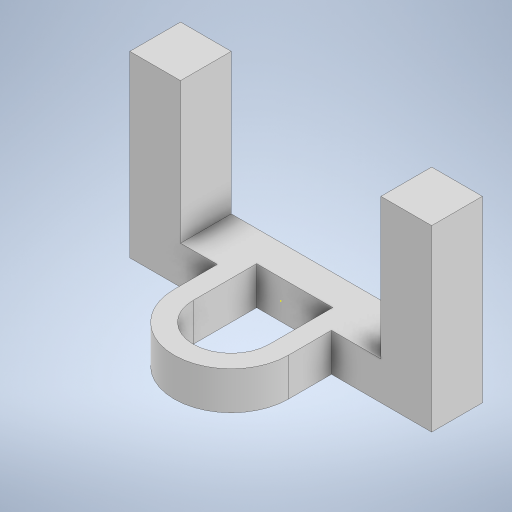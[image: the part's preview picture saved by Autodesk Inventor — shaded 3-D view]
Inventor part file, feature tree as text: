
AUTODESK INVENTOR PART (.ipt)
format: ipt  version: 2024 (Build 280153000, 153)  size: 262,656 bytes
history: native  units: mm
features: sketch x3, extrude x2, other x1
ambient origin geometry x8: Origin, YZ Plane, XZ Plane, XY Plane, X Axis, Y Axis, Z Axis, Center Point
bodies: Body1 (feature_tree)
feature tree (6):
  other  "솔리드1"
  extrude  "돌출1"  Depth=30.0mm
  sketch  "스케치2"
  extrude  "돌출2"  Depth=45.0mm
  sketch  "스케치1"
  sketch  "스케치3"
